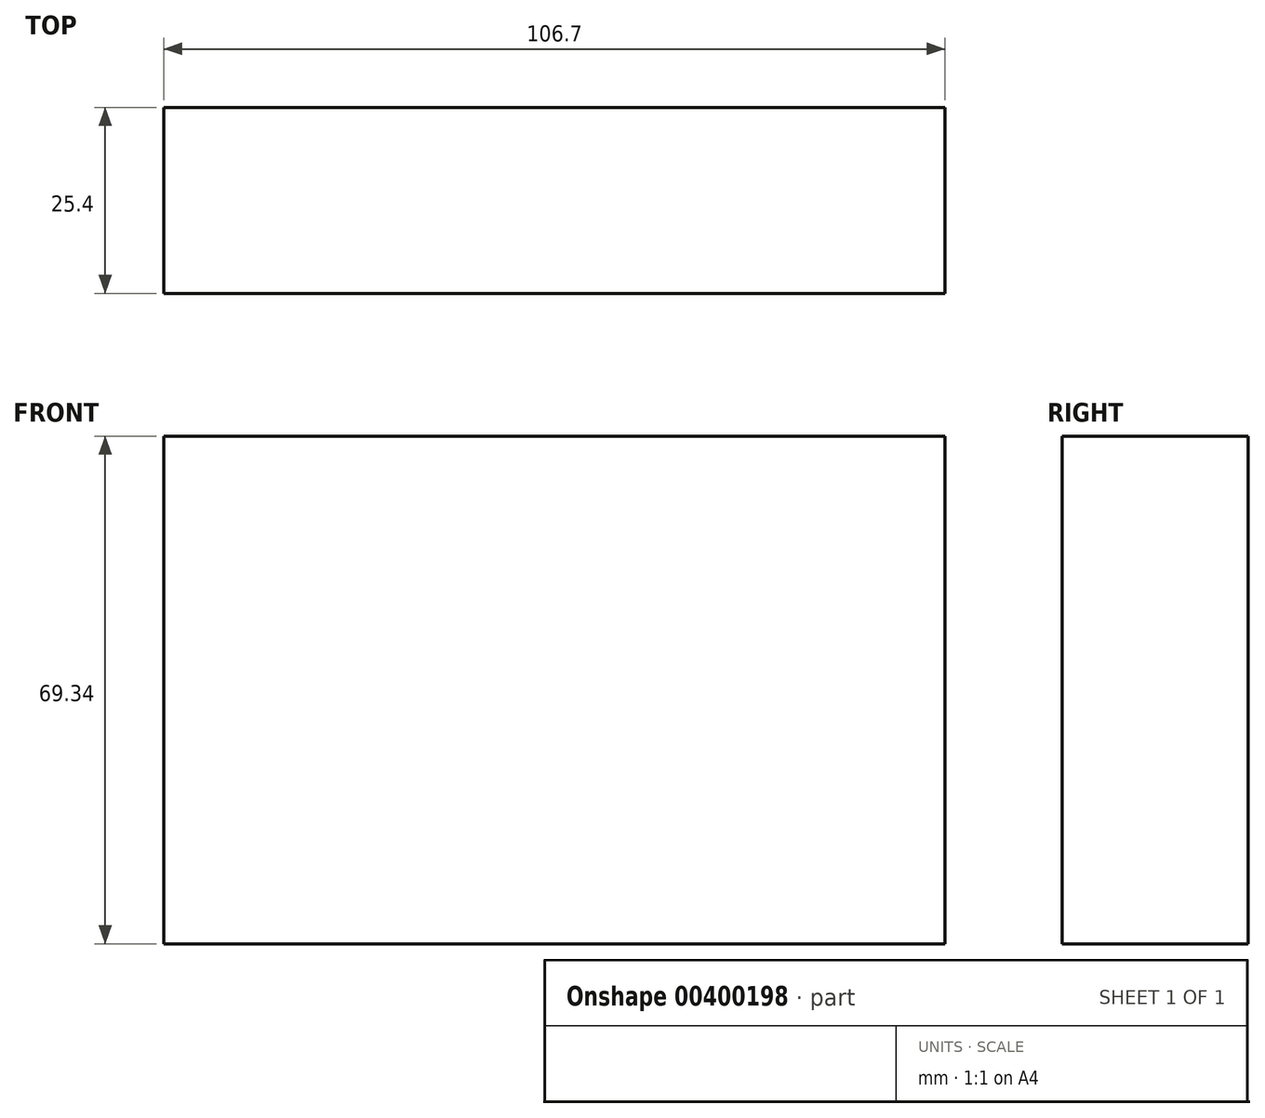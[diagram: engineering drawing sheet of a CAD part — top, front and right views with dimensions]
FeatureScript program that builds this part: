
annotation { "Feature Type Name" : "Feature", "Feature Type Description" : "" }
export const myFeature = defineFeature(function(context is Context, id is Id, definition is map)
    precondition{}
    {
        {
            var Q0;
            Q0=qCreatedBy(makeId("Front.planeOp"),FACE);
            var sketch = newSketch(context, id + "F0", { "sketchPlane" : qUnion([Q0])});
            skLineSegment(sketch, "E0.bottom", {"start": v(53.35, 34.67) * mm, "end": v(-53.35, 34.67) * mm});
            skLineSegment(sketch, "E0.top", {"start": v(53.35, -34.67) * mm, "end": v(-53.35, -34.67) * mm});
            skLineSegment(sketch, "E0.left", {"start": v(53.35, 34.67) * mm, "end": v(53.35, -34.67) * mm});
            skLineSegment(sketch, "E0.right", {"start": v(-53.35, 34.67) * mm, "end": v(-53.35, -34.67) * mm});
            skPoint(sketch, "E0.middle", {"position": v(0, 0) * mm});
            skSolve(sketch);
        }
        {
            var Q0;
            Q0 = qSketchRegion(id + "F0", true);
            extrude(context, id + "F1", {"entities" : qUnion([Q0]), "depth" : 25.4 * mm});
        }
    });
